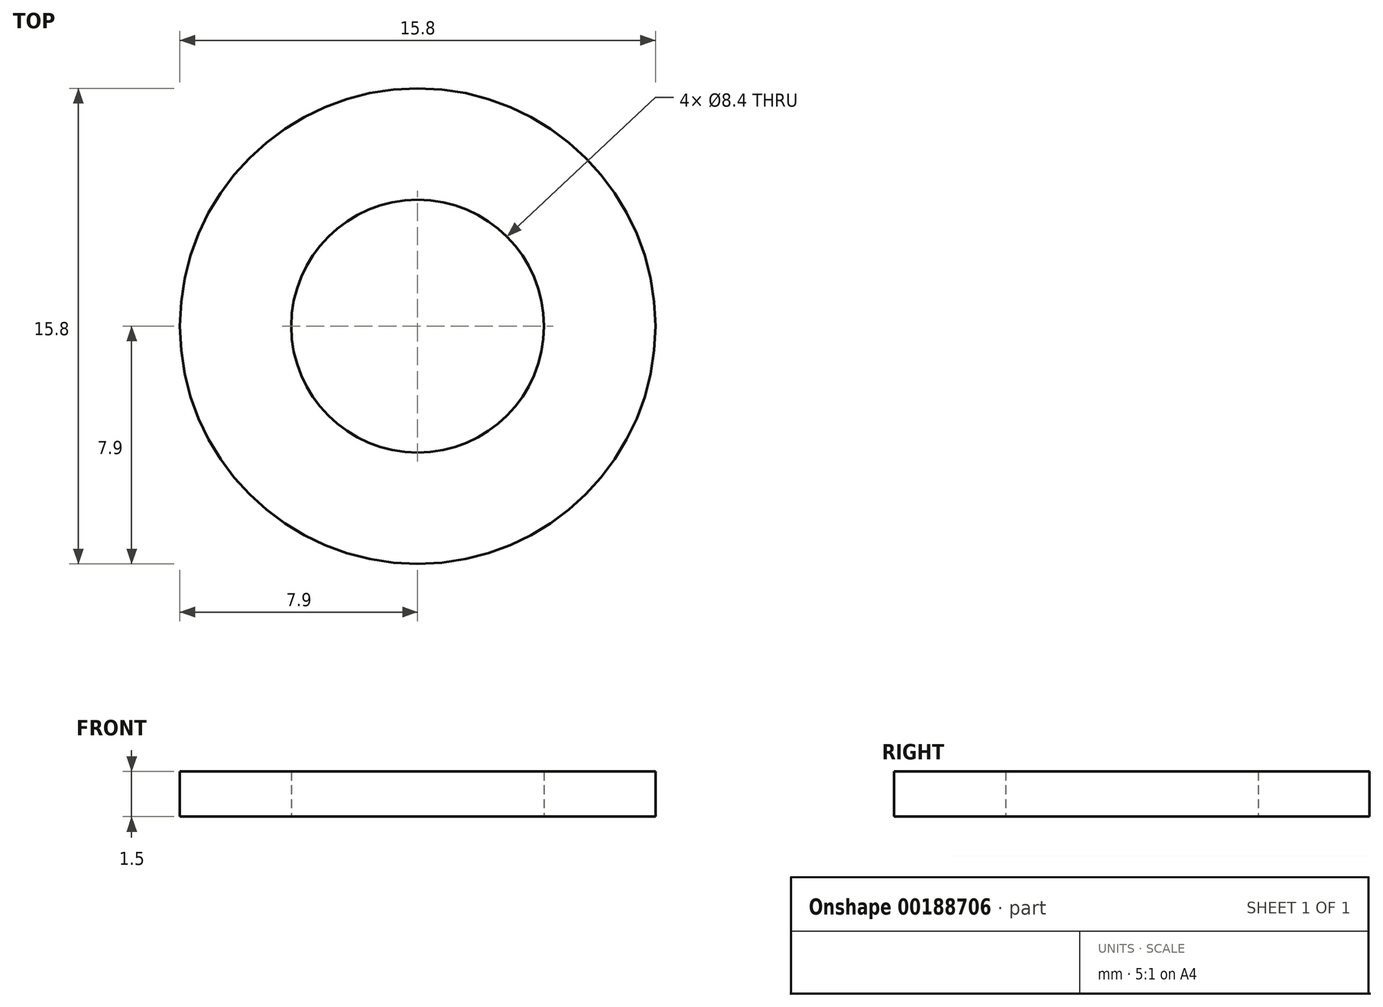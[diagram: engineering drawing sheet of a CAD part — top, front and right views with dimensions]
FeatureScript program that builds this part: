
annotation { "Feature Type Name" : "Feature", "Feature Type Description" : "" }
export const myFeature = defineFeature(function(context is Context, id is Id, definition is map)
    precondition{}
    {
        {
            var Q0;
            Q0=qCreatedBy(makeId("Top.planeOp"),FACE);
            var sketch = newSketch(context, id + "F0", { "sketchPlane" : qUnion([Q0])});
            skCircle(sketch, "E0", {"center": v(0, 0) * mm, "radius": 7.9 * mm});
            skCircle(sketch, "E1", {"center": v(0, 0) * mm, "radius": 4.2 * mm});
            skSolve(sketch);
        }
        {
            var Q0;
            Q0=makeQuery(id+"F0.imprint","IMPRINT",FACE,{"disambiguationData":[TD([[makeQuery(id+"F0.imprint","IMPRINT",EDGE,{"derivedFrom":sQuery(id+"F0.wireOp",EDGE,"E0")}),1.0]])]});
            var Q1;
            Q1=sQuery(id+"F0.wireOp",EDGE,"E0");
            extrude(context, id + "F1", {"entities" : qUnion([Q0]), "surfaceEntities" : qUnion([Q1]), "depth" : 1.5 * mm});
        }
    });
